# Revit family: Fixture_Support_Vertical-Zurn-ZN1202-N4-Narrow-Wall
name_source: partatom
category: Plumbing Fixtures
units: mm (PartAtom-declared; Revit-internal decimal feet)

## family parameters
Always vertical = Yes
Cut with Voids When Loaded = No
Maintain Annotation Orientation = No
OmniClass Number = 23.45.55.11
OmniClass Title = Sanitary Components
Part Type = Normal
Room Calculation Point = No
Round Connector Dimension = Use Radius
Shared = No
Work Plane-Based = No

## types (1)
- Fixture_Support_Vertical-Zurn-ZN1202-N4-Narrow-Wall
    Approx. Weight (Lbs) = 90
    Assembly Code = D2030400
    CW Connection = No
    CWFU = 0
    Default Elevation = 0 "
    Description = NARROW WALL WITH 8-13/16 [224] FRONT TO BACK EZCARRY® ADJUSTABLE VERTICAL HIGHT PERFORMANCE SIPHON JET NO-HUB WATER CLOSET CARRIER SYSTEM
    Distance b/w center of vertical pipe to carrier = 6.625 "
    HW Connection = No
    HWFU = 0
    K DIM = 4.125 "
    Main Material = Iron - Zurn -Cast - Painted - Blue
    Manufacturer = Zurn Water, LLC
    Manufacurer Brand = Zurn
    Model = ZN1202-N4
    Product Documentation Link = https://www.zurn.com
    Product Installation Sheet URL = https://www.zurn.com
    Product Page URL = https://www.zurn.com
    Product data url = https://www.bimobject.com
    Sanitary Inlet Radius = 2 "
    Sanitary Outlet Radius = 2 "
    URL = www.zurn.com
    Vent Connection = Yes
    Vent Connection Radius = 1 "
    Vent Diameter (Actual) = 2.375 "
    Vent Diameter (Nominal) = 2 "
    Vertical Pipe Diameter (Actual) = 4.5 "
    Vertical Pipe Diameter (Nominal) = 4 "
    Vertical Pipe Length = 24 "
    WFU = 0
    Waste Connection = Yes
    Water Closet Inlet Radius = 1.5 "

## geometry (parser evidence)
native form markers: Sweep x4
no freeform markers — native parametric forms only
